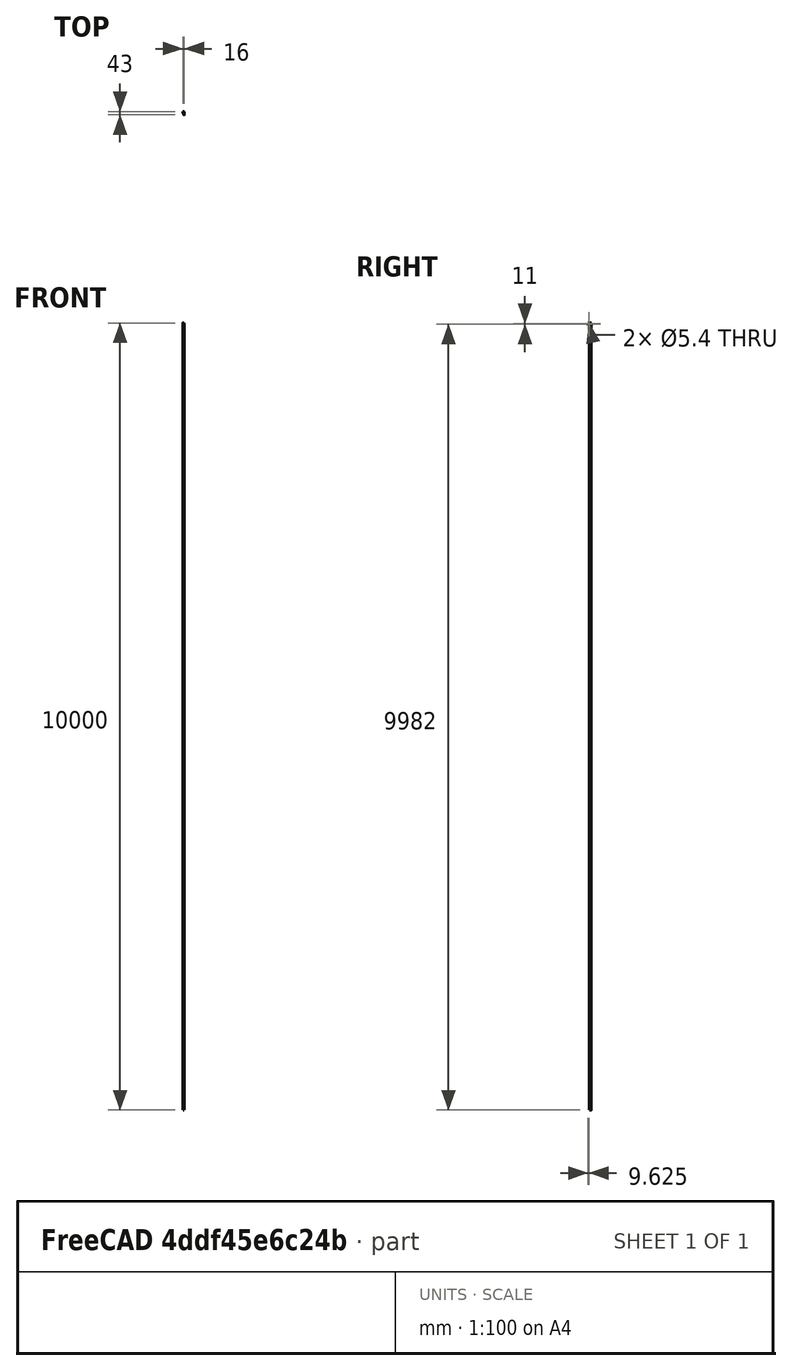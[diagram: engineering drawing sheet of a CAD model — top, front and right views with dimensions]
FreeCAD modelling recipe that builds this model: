
FCSTD DOCUMENT  (FreeCAD 0.16R)
Label: RackHook
License: All rights reserved
LicenseURL: http://en.wikipedia.org/wiki/All_rights_reserved
objects: Sketcher::SketchObject×8, PartDesign::Pocket×4, PartDesign::Pad×3, PartDesign::Fillet×1, Mesh::Feature×1
note: 23 computed .brp shape members not serialized (recipe doc carries the construction recipe); baked Part::Feature solids carry a one-line shape summary decoded from their .brp

FEATURE [Sketcher::SketchObject] Sketch
FEATURE [Sketcher::SketchObject] Sketch001
  sketch-geometry (2):
    g0: Circle [constr] CenterX=0 CenterY=0 CenterZ=0 NormalX=0 NormalY=0 NormalZ=1 Radius=4
    g1: Circle CenterX=0 CenterY=0 CenterZ=0 NormalX=0 NormalY=0 NormalZ=1 Radius=8
  constraints (4):
    c: Coincident(g0,g-1)
    c: Radius(g0) = 4
    c: Coincident(g1,g-1)
    c: Radius(g1) = 8
FEATURE [PartDesign::Pad] Pad
  Length = 25
  Length2 = 100
  Sketch = -> Sketch001
  Type = 0
FEATURE [Sketcher::SketchObject] Sketch002
  ExternalGeometry = -> [Pad]
  Placement = pos=(0,0,25) rot=(0,0,1;0rad)
  Support = -> Pad [Face3]
  sketch-geometry (4):
    g0: LineSegment StartX=4 StartY=0 StartZ=0 EndX=8 EndY=0 EndZ=0
    g1: LineSegment StartX=8 StartY=0 StartZ=0 EndX=8 EndY=-35 EndZ=0
    g2: LineSegment StartX=8 StartY=-35 StartZ=0 EndX=4 EndY=-35 EndZ=0
    g3: LineSegment StartX=4 StartY=-35 StartZ=0 EndX=4 EndY=0 EndZ=0
  constraints (12):
    c: Coincident(g0,g1)
    c: Coincident(g1,g2)
    c: Coincident(g2,g3)
    c: Coincident(g3,g0)
    c: Horizontal(g0)
    c: Horizontal(g2)
    c: Vertical(g1)
    c: Vertical(g3)
    c: PointOnObject(g0,g-3)
    c: PointOnObject(g0,g-1)
    c: Distance(g2) = 4
    c: Distance(g1) = 35
FEATURE [PartDesign::Pad] Pad001
  Length = 25
  Length2 = 100
  Reversed = true
  Sketch = -> Sketch002
  Type = 0
FEATURE [Sketcher::SketchObject] Sketch003
  ExternalGeometry = -> [Pad001]
  Placement = pos=(0,0,25) rot=(0,0,1;0rad)
  Support = -> Pad001 [Face10]
  sketch-geometry (4):
    g0: LineSegment StartX=-8 StartY=0 StartZ=0 EndX=-4 EndY=0 EndZ=0
    g1: LineSegment StartX=-4 StartY=0 StartZ=0 EndX=-1.5 EndY=-11.7367 EndZ=0
    g2: LineSegment StartX=-1.5 StartY=-11.7367 StartZ=0 EndX=-5.5 EndY=-11.7367 EndZ=0
    g3: LineSegment StartX=-5.5 StartY=-11.7367 StartZ=0 EndX=-8 EndY=0 EndZ=0
  constraints (12):
    c: Coincident(g0,g1)
    c: Coincident(g1,g2)
    c: Coincident(g2,g3)
    c: Coincident(g3,g0)
    c: Horizontal(g0)
    c: PointOnObject(g0,g-1)
    c: PointOnObject(g0,g-3)
    c: Distance(g0) = 4
    c: Parallel(g3,g1)
    c: DistanceX(g1) = -1.5
    c: Distance(g3) = 12
    c: Horizontal(g2)
FEATURE [PartDesign::Pad] Pad002
  Length = 25
  Length2 = 100
  Reversed = true
  Sketch = -> Sketch003
  Type = 0
FEATURE [Sketcher::SketchObject] Sketch004
  Placement = pos=(0,0,25) rot=(0,0,1;0rad)
  Support = -> Pad002 [Face12]
  sketch-geometry (1):
    g0: Circle CenterX=0 CenterY=0 CenterZ=0 NormalX=0 NormalY=0 NormalZ=1 Radius=4
  constraints (2):
    c: Radius(g0) = 4
    c: Coincident(g0,g-1)
FEATURE [PartDesign::Pocket] Pocket
  Length = 5
  Sketch = -> Sketch004
  Type = 1
FEATURE [Sketcher::SketchObject] Sketch005
  ExternalGeometry = -> [Pocket]
  Placement = pos=(0,0,25) rot=(0,0,1;0rad)
  Support = -> Pocket [Face12]
  sketch-geometry (4):
    g0: LineSegment StartX=-4 StartY=0 StartZ=0 EndX=-0.635854 EndY=-15.7936 EndZ=0
    g1: LineSegment StartX=-0.635854 StartY=-15.7936 StartZ=0 EndX=4 EndY=-15.7936 EndZ=0
    g2: LineSegment StartX=4 StartY=-15.7936 StartZ=0 EndX=4 EndY=0 EndZ=0
    g3: LineSegment StartX=-4 StartY=0 StartZ=0 EndX=4 EndY=0 EndZ=0
  constraints (11):
    c: PointOnObject(g0,g-1)
    c: Coincident(g0,g1)
    c: Horizontal(g1)
    c: Coincident(g1,g2)
    c: Coincident(g0,g-5)
    c: Coincident(g2,g-5)
    c: PointOnObject(g-3,g0)
    c: PointOnObject(g1,g-4)
    c: Coincident(g3,g0)
    c: Coincident(g3,g2)
    c: Distance(g0) = 16.1479
FEATURE [PartDesign::Pocket] Pocket001
  Length = 5
  Sketch = -> Sketch005
  Type = 1
FEATURE [Sketcher::SketchObject] Sketch006
  Placement = pos=(8,0,0) rot=(0.57735,0.57735,0.57735;2.0944rad)
  Support = -> Pocket001 [Face2]
  sketch-geometry (2):
    g0: Circle CenterX=-25.3745 CenterY=7 CenterZ=0 NormalX=0 NormalY=0 NormalZ=1 Radius=2.7
    g1: Circle CenterX=-25.3745 CenterY=18 CenterZ=0 NormalX=0 NormalY=0 NormalZ=1 Radius=2.7
  constraints (5):
    c: Radius(g0) = 2.7
    c: Equal(g0,g1)
    c: Distance(g0,g1) = 11
    c: DistanceX(g0,g1) = 0
    c: DistanceY(g0) = 7
FEATURE [PartDesign::Pocket] Pocket002
  Length = 5
  Sketch = -> Sketch006
  Type = 0
FEATURE [Sketcher::SketchObject] Sketch007
  ExternalGeometry = -> [Pocket002]
  Placement = pos=(4,0,0) rot=(0.57735,-0.57735,-0.57735;2.0944rad)
  Support = -> Pocket002 [Face3]
  sketch-geometry (14):
    g0: LineSegment StartX=20.6114 StartY=18 StartZ=0 EndX=22.9929 EndY=13.875 EndZ=0
    g1: LineSegment StartX=22.9929 StartY=13.875 StartZ=0 EndX=27.7561 EndY=13.875 EndZ=0
    g2: LineSegment StartX=27.7561 StartY=13.875 StartZ=0 EndX=30.1377 EndY=18 EndZ=0
    g3: LineSegment StartX=30.1377 StartY=18 StartZ=0 EndX=27.7561 EndY=22.125 EndZ=0
    g4: LineSegment StartX=27.7561 StartY=22.125 StartZ=0 EndX=22.9929 EndY=22.125 EndZ=0
    g5: LineSegment StartX=22.9929 StartY=22.125 StartZ=0 EndX=20.6114 EndY=18 EndZ=0
    g6: Circle [constr] CenterX=25.3745 CenterY=18 CenterZ=0 NormalX=0 NormalY=0 NormalZ=1 Radius=4.76314
    g7: LineSegment StartX=27.7561 StartY=2.875 StartZ=0 EndX=30.1377 EndY=7 EndZ=0
    g8: LineSegment StartX=30.1377 StartY=7 StartZ=0 EndX=27.7561 EndY=11.125 EndZ=0
    g9: LineSegment StartX=27.7561 StartY=11.125 StartZ=0 EndX=22.9929 EndY=11.125 EndZ=0
    g10: LineSegment StartX=22.9929 StartY=11.125 StartZ=0 EndX=20.6114 EndY=7 EndZ=0
    g11: LineSegment StartX=20.6114 StartY=7 StartZ=0 EndX=22.9929 EndY=2.875 EndZ=0
    g12: LineSegment StartX=22.9929 StartY=2.875 StartZ=0 EndX=27.7561 EndY=2.875 EndZ=0
    g13: Circle [constr] CenterX=25.3745 CenterY=7 CenterZ=0 NormalX=0 NormalY=0 NormalZ=1 Radius=4.76314
  constraints (32):
    c: Coincident(g0,g1)
    c: Coincident(g1,g2)
    c: Coincident(g2,g3)
    c: Coincident(g3,g4)
    c: Coincident(g4,g5)
    c: Coincident(g5,g0)
    c: Equal(g0, g1-g5) x5
    c: PointOnObject(g0,g6)
    c: PointOnObject(g1,g6)
    c: PointOnObject(g2,g6)
    c: PointOnObject(g3,g6)
    c: PointOnObject(g4,g6)
    c: PointOnObject(g5,g6)
    c: Coincident(g7,g8)
    c: Coincident(g8,g9)
    c: Coincident(g9,g10)
    c: Coincident(g10,g11)
    c: Coincident(g11,g12)
    c: Coincident(g12,g7)
    c: Equal(g7, g8-g12) x5
    c: PointOnObject(g7,g13)
    c: PointOnObject(g8,g13)
    c: PointOnObject(g9,g13)
    c: PointOnObject(g10,g13)
    c: PointOnObject(g11,g13)
    c: PointOnObject(g12,g13)
    c: Distance(g7,g11) = 8.25
    c: Distance(g0,g1) = 8.25
    c: Coincident(g6,g-3)
    c: Coincident(g13,g-4)
    c: Horizontal(g9)
    c: Horizontal(g1)
FEATURE [PartDesign::Pocket] Pocket003
  Length = 1
  Sketch = -> Sketch007
  Type = 0
FEATURE [PartDesign::Fillet] Fillet
  Base = -> Pocket003 [Edge80,Edge91,Edge2,Edge1]
  Radius = 1
FEATURE [Mesh::Feature] Mesh  label="Fillet (Meshed)"
